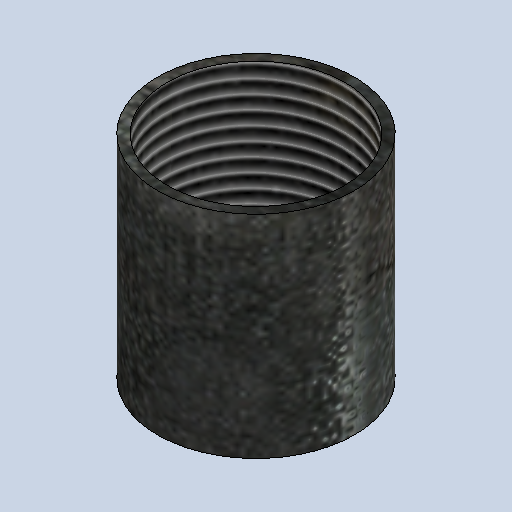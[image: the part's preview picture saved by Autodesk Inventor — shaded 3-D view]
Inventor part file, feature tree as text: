
AUTODESK INVENTOR PART (.ipt)
format: ipt  version: 2025.1 (Build 291241020, 241B)  size: 275,456 bytes
history: native  units: mm
features: sketch x2, extrude x1, hole x1
ambient origin geometry x8: Origin, YZ Plane, XZ Plane, XY Plane, X Axis, Y Axis, Z Axis, Center Point
bodies: Solid1 (feature_tree)
feature tree (4):
  extrude  "Extrusion1"  Depth=36.0mm TaperAngle=0.0deg
  hole  "Hole1"  [1 undecoded]
  sketch  "Sketch1"  dims[d0=33.5mm d1=36.0mm d2=0.0mm]
  sketch  "Sketch2"  dims[d3=30.291mm d4=66.498mm d5=4.0mm d6=2.0mm d7=90.0deg d8=8.0mm d9=20.594885mm]
note: 1 required parameter value undecoded (feature->parameter linkage not recoverable at this tier; creation-order binding heuristic only, values carry confidence <= 0.55)
